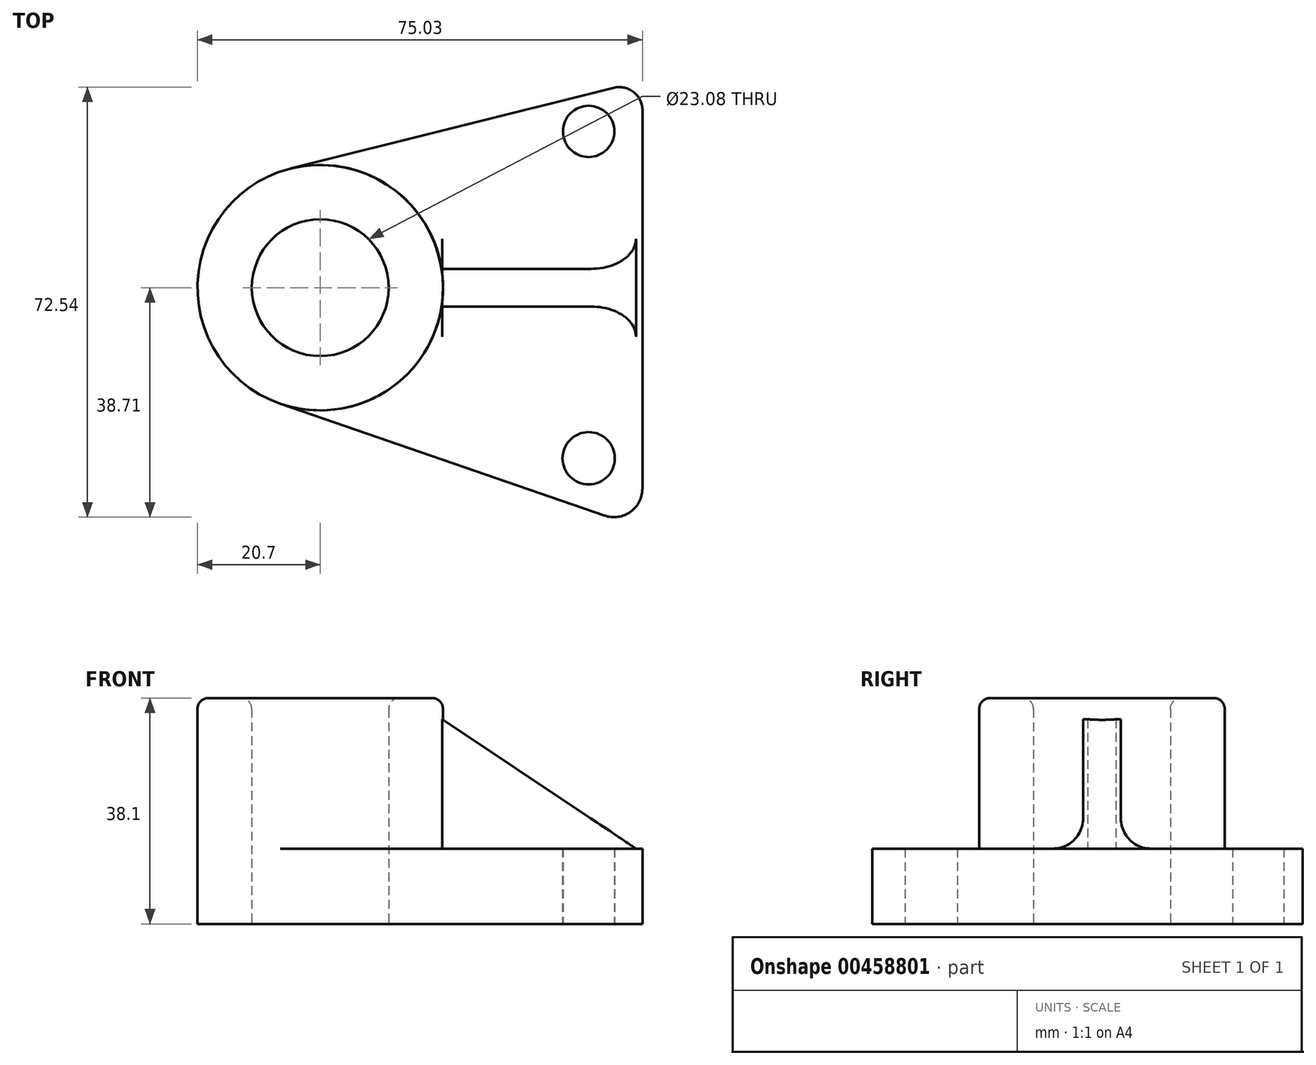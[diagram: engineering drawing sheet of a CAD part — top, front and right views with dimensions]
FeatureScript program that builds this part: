
annotation { "Feature Type Name" : "Feature", "Feature Type Description" : "" }
export const myFeature = defineFeature(function(context is Context, id is Id, definition is map)
    precondition{}
    {
        {
            var Q0;
            Q0=qCreatedBy(makeId("Top.planeOp"),FACE);
            var sketch = newSketch(context, id + "F0", { "sketchPlane" : qUnion([Q0])});
            skCircle(sketch, "E0", {"center": v(0, 0) * mm, "radius": 11.54 * mm});
            skCircle(sketch, "E1", {"center": v(0, 0) * mm, "radius": 20.7 * mm});
            skLineSegment(sketch, "E2", {"start": v(-6.75, -19.57) * mm, "end": v(47.96, -38.44) * mm});
            skLineSegment(sketch, "E3", {"start": v(-5.02, 20.08) * mm, "end": v(49.47, 33.72) * mm});
            skArc(sketch, "E4", {"start": v(49.47, 33.72) * mm, "mid": v(52.82, 33) * mm, "end": v(54.33, 29.92) * mm});
            skArc(sketch, "E5", {"start": v(47.96, -38.44) * mm, "mid": v(52.31, -37.81) * mm, "end": v(54.33, -33.9) * mm});
            skLineSegment(sketch, "E6", {"start": v(54.33, 29.92) * mm, "end": v(54.33, -33.9) * mm});
            skCircle(sketch, "E7", {"center": v(45.27, -28.77) * mm, "radius": 4.41 * mm});
            skCircle(sketch, "E8", {"center": v(45.27, 26.36) * mm, "radius": 4.33 * mm});
            skSolve(sketch);
        }
        {
            var Q0;
            Q0=makeQuery(id+"F0.imprint","IMPRINT",FACE,{"disambiguationData":[TD([[makeQuery(id+"F0.imprint","IMPRINT",EDGE,{"derivedFrom":sQuery(id+"F0.wireOp",EDGE,"E0")}),-1.0]])]});
            var Q1;
            {var subQ4=sQuery(id+"F0.wireOp",EDGE,"mxLrC7Qq-0sGQ-6ssc-yDJz-oNrBYB4zYiSv");Q1=makeQuery(id+"F0.imprint","IMPRINT",FACE,{"disambiguationData":[TD([[makeQuery(id+"F0.imprint","IMPRINT",EDGE,{"derivedFrom":subQ4}),1.0]])]});}
            var Q2;
            {var subQ1=sQuery(id+"F0.wireOp",EDGE,"u73swnTY-pMc7-lH2V-4T1l-oWxjisXigy7F");Q2=makeQuery(id+"F0.imprint","IMPRINT",FACE,{"disambiguationData":[TD([[makeQuery(id+"F0.imprint","IMPRINT",EDGE,{"derivedFrom":subQ1}),-1.0]])]});}
            extrude(context, id + "F1", {"entities" : qUnion([Q0, Q1, Q2]), "depth" : 12.7 * mm});
        }
        {
            var Q0;
            Q0=makeQuery(id+"F0.imprint","IMPRINT",FACE,{"disambiguationData":[TD([[makeQuery(id+"F0.imprint","IMPRINT",EDGE,{"derivedFrom":sQuery(id+"F0.wireOp",EDGE,"E0")}),-1.0]])]});
            extrude(context, id + "F2", {"entities" : qUnion([Q0]), "operationType" : NewBodyOperationType.ADD, "depth" : 38.1 * mm});
        }
        {
            var Q0;
            Q0=makeQuery(id+"F2.opExtrude","CAP_EDGE",EDGE,{"disambiguationData":[OSD([sQuery(id+"F0.wireOp",EDGE,"E1")])],"isStart":false});
            var Q1;
            Q1=makeQuery(id+"F2.opExtrude","CAP_EDGE",EDGE,{"disambiguationData":[OSD([sQuery(id+"F0.wireOp",EDGE,"E0")])],"isStart":false});
            fillet(context, id + "F3", {"entities" : qUnion([Q0, Q1]), "radius" : 1.84 * mm, "tangentPropagation" : true, "allowEdgeOverflow" : false});
        }
        {
            var Q0;
            {var subQ1=sQuery(id+"F0.wireOp",EDGE,"E2");Q0=makeQuery(id+"F0.imprint","IMPRINT",FACE,{"disambiguationData":[TD([[makeQuery(id+"F0.imprint","IMPRINT",EDGE,{"derivedFrom":subQ1}),1.0]])]});}
            extrude(context, id + "F4", {"entities" : qUnion([Q0]), "operationType" : NewBodyOperationType.ADD, "depth" : 12.7 * mm});
        }
        {
            var Q0;
            Q0=qCreatedBy(makeId("Front.planeOp"),FACE);
            var sketch = newSketch(context, id + "F5", { "sketchPlane" : qUnion([Q0])});
            skLineSegment(sketch, "E9", {"start": v(20.56, 34.5) * mm, "end": v(53.42, 12.59) * mm});
            skLineSegment(sketch, "E10", {"start": v(53.42, 12.59) * mm, "end": v(20.56, 12.59) * mm});
            skLineSegment(sketch, "E11", {"start": v(20.56, 12.59) * mm, "end": v(20.56, 34.5) * mm});
            skSolve(sketch);
        }
        {
            var Q0;
            Q0=makeQuery(id+"F5.imprint","IMPRINT",FACE,{"disambiguationData":[TD([[makeQuery(id+"F5.imprint","IMPRINT",EDGE,{"derivedFrom":sQuery(id+"F5.wireOp",EDGE,"E9")}),-1.0]])]});
            extrude(context, id + "F6", {"entities" : qUnion([Q0]), "operationType" : NewBodyOperationType.ADD, "depth" : 6.35 * mm, "symmetric" : true});
        }
        {
            var Q0;
            {var subQ0=sQuery(id+"F0.wireOp",EDGE,"E2");var subQ1=sQuery(id+"F0.wireOp",EDGE,"E1");Q0=makeQuery(id+"F6.boolean.opBoolean","SPLIT",EDGE,{"disambiguationData":[TD([makeQuery(id+"F4.opExtrude","SWEPT_FACE",FACE,{"disambiguationData":[OSD([subQ0])]})])],"derivedFrom":makeQuery(id+"F4.opExtrude","CAP_EDGE",EDGE,{"disambiguationData":[OSD([subQ1])],"isStart":false})});}
            var Q1;
            {var subQ0=sQuery(id+"F0.wireOp",EDGE,"E3");var subQ1=sQuery(id+"F0.wireOp",EDGE,"E1");Q1=makeQuery(id+"F6.boolean.opBoolean","SPLIT",EDGE,{"disambiguationData":[TD([makeQuery(id+"F4.opExtrude","SWEPT_FACE",FACE,{"disambiguationData":[OSD([subQ0])]})])],"derivedFrom":makeQuery(id+"F4.opExtrude","CAP_EDGE",EDGE,{"disambiguationData":[OSD([subQ1])],"isStart":false})});}
            var Q2;
            Q2=makeQuery(id+"F6.boolean.opBoolean","INTERSECT",EDGE,{"derivedFrom":[makeQuery(id+"F4.opExtrude","CAP_FACE",FACE,{"disambiguationData":[OSD([sQuery(id+"F0.wireOp",EDGE,"E1"),sQuery(id+"F0.wireOp",EDGE,"E2"),sQuery(id+"F0.wireOp",EDGE,"E3"),sQuery(id+"F0.wireOp",EDGE,"E4"),sQuery(id+"F0.wireOp",EDGE,"E5"),sQuery(id+"F0.wireOp",EDGE,"E6"),sQuery(id+"F0.wireOp",EDGE,"E7"),sQuery(id+"F0.wireOp",EDGE,"E8")])],"isStart":false}),makeQuery(id+"F6.opExtrude","CAP_FACE",FACE,{"disambiguationData":[OSD([sQuery(id+"F5.wireOp",EDGE,"E9"),sQuery(id+"F5.wireOp",EDGE,"E10"),sQuery(id+"F5.wireOp",EDGE,"E11")])],"isStart":false})]});
            var Q3;
            Q3=makeQuery(id+"F6.boolean.opBoolean","INTERSECT",EDGE,{"derivedFrom":[makeQuery(id+"F4.opExtrude","CAP_FACE",FACE,{"disambiguationData":[OSD([sQuery(id+"F0.wireOp",EDGE,"E1"),sQuery(id+"F0.wireOp",EDGE,"E2"),sQuery(id+"F0.wireOp",EDGE,"E3"),sQuery(id+"F0.wireOp",EDGE,"E4"),sQuery(id+"F0.wireOp",EDGE,"E5"),sQuery(id+"F0.wireOp",EDGE,"E6"),sQuery(id+"F0.wireOp",EDGE,"E7"),sQuery(id+"F0.wireOp",EDGE,"E8")])],"isStart":false}),makeQuery(id+"F6.opExtrude","CAP_FACE",FACE,{"disambiguationData":[OSD([sQuery(id+"F5.wireOp",EDGE,"E9"),sQuery(id+"F5.wireOp",EDGE,"E10"),sQuery(id+"F5.wireOp",EDGE,"E11")])],"isStart":true})]});
            fillet(context, id + "F7", {"entities" : qUnion([Q0, Q1, Q2, Q3]), "radius" : 5.08 * mm, "tangentPropagation" : true, "allowEdgeOverflow" : false});
        }
    });
